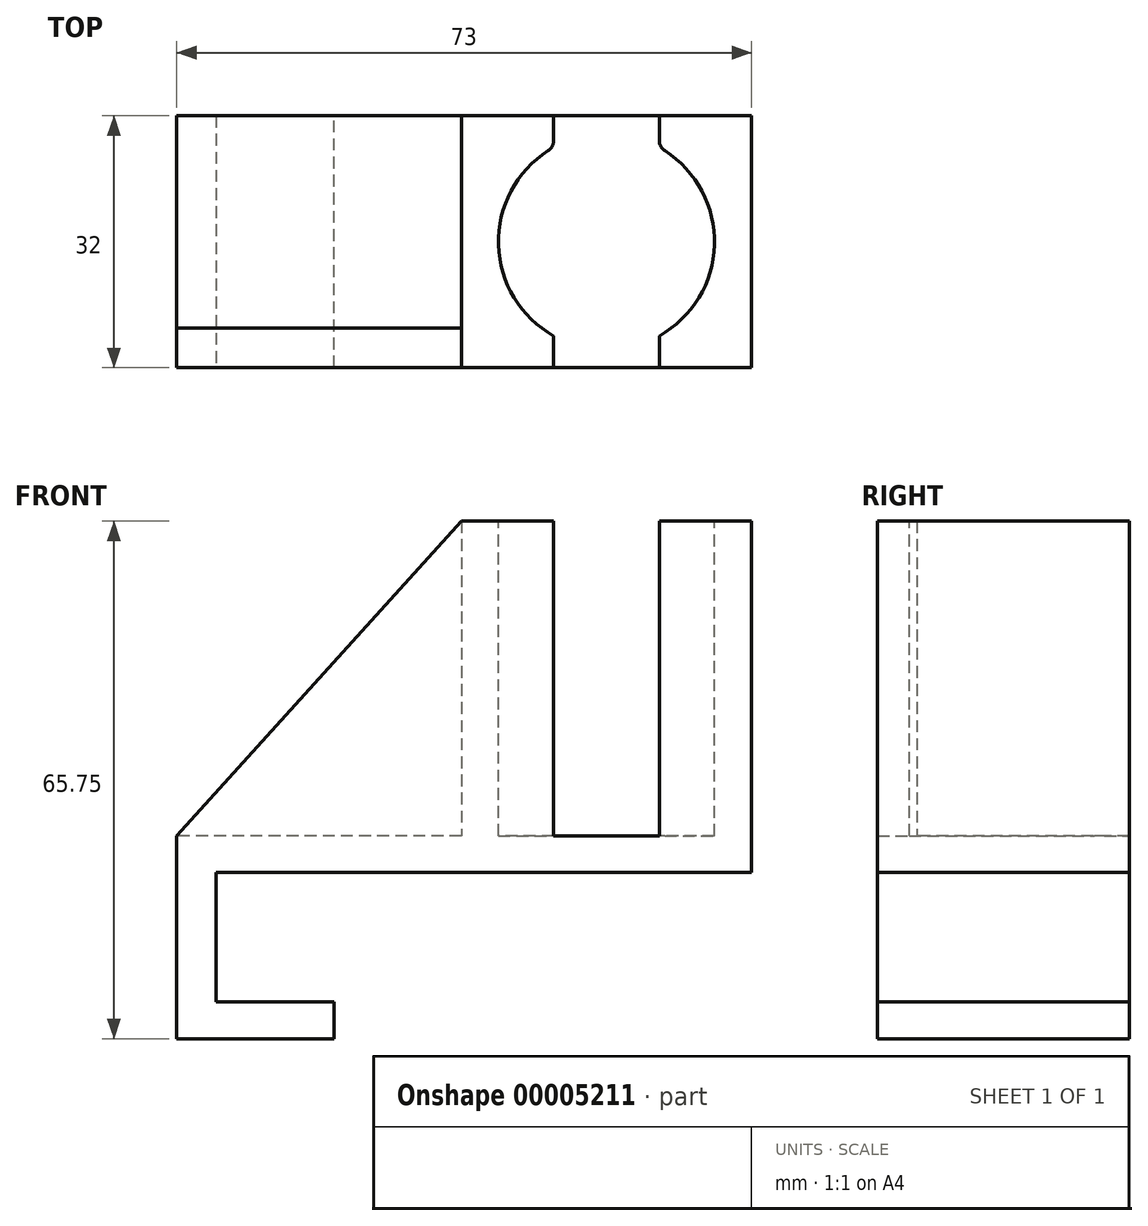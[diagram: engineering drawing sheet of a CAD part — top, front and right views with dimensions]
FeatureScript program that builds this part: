
annotation { "Feature Type Name" : "Feature", "Feature Type Description" : "" }
export const myFeature = defineFeature(function(context is Context, id is Id, definition is map)
    precondition{}
    {
        {
            var Q0;
            Q0=qCreatedBy(makeId("Front.planeOp"),FACE);
            var sketch = newSketch(context, id + "F0", { "sketchPlane" : qUnion([Q0])});
            skLineSegment(sketch, "E0.bottom", {"start": v(0, 0) * mm, "end": v(84, 0) * mm});
            skLineSegment(sketch, "E0.top", {"start": v(0, 15.75) * mm, "end": v(84, 15.75) * mm});
            skLineSegment(sketch, "E0.left", {"start": v(0, 0) * mm, "end": v(0, 15.75) * mm});
            skLineSegment(sketch, "E0.right", {"start": v(84, 0) * mm, "end": v(84, 15.75) * mm, "construction": true});
            skLineSegment(sketch, "E1", {"start": v(84, 15.75) * mm, "end": v(84, 20.75) * mm});
            skLineSegment(sketch, "E2", {"start": v(84, 20.75) * mm, "end": v(-5, 20.75) * mm});
            skLineSegment(sketch, "E3", {"start": v(-5, 20.75) * mm, "end": v(-5, -5) * mm});
            skLineSegment(sketch, "E4", {"start": v(-5, -5) * mm, "end": v(84, -5) * mm});
            skLineSegment(sketch, "E5", {"start": v(84, -5) * mm, "end": v(84, 0) * mm});
            skLineSegment(sketch, "E6", {"start": v(0, 15.75) * mm, "end": v(-5, 15.75) * mm, "construction": true});
            skSolve(sketch);
        }
        {
            var Q0;
            Q0 = qSketchRegion(id + "F0", true);
            extrude(context, id + "F1", {"entities" : qUnion([Q0]), "depth" : 32 * mm, "offsetDistance" : 25 * mm});
        }
        {
            var Q0;
            Q0=makeQuery(id+"F1.opExtrude","CAP_FACE",FACE,{"disambiguationData":[OSD([sQuery(id+"F0.wireOp",EDGE,"E0.bottom"),sQuery(id+"F0.wireOp",EDGE,"E0.top"),sQuery(id+"F0.wireOp",EDGE,"E0.left"),sQuery(id+"F0.wireOp",EDGE,"E1"),sQuery(id+"F0.wireOp",EDGE,"E2"),sQuery(id+"F0.wireOp",EDGE,"E3"),sQuery(id+"F0.wireOp",EDGE,"E4"),sQuery(id+"F0.wireOp",EDGE,"E5")])],"isStart":false});
            var sketch = newSketch(context, id + "F2", { "sketchPlane" : qUnion([Q0])});
            skLineSegment(sketch, "E7.bottom", {"start": v(84, 0) * mm, "end": v(15, 0) * mm});
            skLineSegment(sketch, "E7.top", {"start": v(84, -5) * mm, "end": v(15, -5) * mm});
            skLineSegment(sketch, "E7.left", {"start": v(84, 0) * mm, "end": v(84, -5) * mm});
            skLineSegment(sketch, "E7.right", {"start": v(15, 0) * mm, "end": v(15, -5) * mm});
            skSolve(sketch);
        }
        {
            var Q0;
            Q0 = qSketchRegion(id + "F2", true);
            extrude(context, id + "F3", {"entities" : qUnion([Q0]), "operationType" : NewBodyOperationType.REMOVE, "endBound" : BoundingType.THROUGH_ALL, "oppositeDirection" : true, "depth" : 25 * mm, "offsetDistance" : 25 * mm});
        }
        {
            var Q0;
            Q0=makeQuery(id+"F1.opExtrude","SWEPT_FACE",FACE,{"disambiguationData":[OSD([sQuery(id+"F0.wireOp",EDGE,"E2")])]});
            var sketch = newSketch(context, id + "F4", { "sketchPlane" : qUnion([Q0])});
            skCircle(sketch, "E8", {"center": v(49.58, -16) * mm, "radius": 13.43 * mm, "construction": true});
            skCircle(sketch, "E9", {"center": v(49.58, -16) * mm, "radius": 34.42 * mm, "construction": true});
            skLineSegment(sketch, "E10", {"start": v(49.58, -16) * mm, "end": v(15.15, -16) * mm, "construction": true});
            skLineSegment(sketch, "E11", {"start": v(15.15, -16) * mm, "end": v(-5, -16) * mm, "construction": true});
            skLineSegment(sketch, "E12", {"start": v(49.58, -16) * mm, "end": v(49.58, 0) * mm, "construction": true});
            skArc(sketch, "E13", {"start": v(42.86, -27.63) * mm, "mid": v(36.15, -16) * mm, "end": v(42.86, -4.37) * mm});
            skLineSegment(sketch, "E14", {"start": v(42.86, -4.37) * mm, "end": v(42.86, 0) * mm});
            skLineSegment(sketch, "E15", {"start": v(42.86, 0) * mm, "end": v(31.15, 0) * mm});
            skLineSegment(sketch, "E16", {"start": v(31.15, 0) * mm, "end": v(31.15, -32) * mm});
            skLineSegment(sketch, "E17", {"start": v(31.15, -32) * mm, "end": v(42.86, -32) * mm});
            skLineSegment(sketch, "E18", {"start": v(42.86, -32) * mm, "end": v(42.86, -27.63) * mm});
            skLineSegment(sketch, "E19", {"start": v(42.86, -4.37) * mm, "end": v(49.58, -16) * mm, "construction": true});
            skArc(sketch, "E20.MirrorCS", {"start": v(56.29, -27.63) * mm, "mid": v(63, -16) * mm, "end": v(56.29, -4.37) * mm});
            skLineSegment(sketch, "E21.MirrorCS", {"start": v(56.29, -32) * mm, "end": v(56.29, -27.63) * mm});
            skLineSegment(sketch, "E22.MirrorCS", {"start": v(68, -32) * mm, "end": v(56.29, -32) * mm});
            skLineSegment(sketch, "E23.MirrorCS", {"start": v(68, 0) * mm, "end": v(68, -32) * mm});
            skLineSegment(sketch, "E24.MirrorCS", {"start": v(56.29, 0) * mm, "end": v(68, 0) * mm});
            skLineSegment(sketch, "E25.MirrorCS", {"start": v(56.29, -4.37) * mm, "end": v(56.29, 0) * mm});
            skSolve(sketch);
        }
        {
            var Q0;
            Q0 = qSketchRegion(id + "F4", true);
            extrude(context, id + "F5", {"entities" : qUnion([Q0]), "operationType" : NewBodyOperationType.ADD, "depth" : 40 * mm, "offsetDistance" : 25 * mm});
        }
        {
            var Q0;
            Q0=makeQuery(id+"F5.boolean.opBoolean","MERGE",FACE,{"derivedFrom":[makeQuery(id+"F1.opExtrude","CAP_FACE",FACE,{"disambiguationData":[OSD([sQuery(id+"F0.wireOp",EDGE,"E0.bottom"),sQuery(id+"F0.wireOp",EDGE,"E0.top"),sQuery(id+"F0.wireOp",EDGE,"E0.left"),sQuery(id+"F0.wireOp",EDGE,"E1"),sQuery(id+"F0.wireOp",EDGE,"E2"),sQuery(id+"F0.wireOp",EDGE,"E3"),sQuery(id+"F0.wireOp",EDGE,"E4"),sQuery(id+"F0.wireOp",EDGE,"E5")])],"isStart":false}),makeQuery(id+"F5.opExtrude","SWEPT_FACE",FACE,{"disambiguationData":[OSD([sQuery(id+"F4.wireOp",EDGE,"E17")])]}),makeQuery(id+"F5.opExtrude","SWEPT_FACE",FACE,{"disambiguationData":[OSD([sQuery(id+"F4.wireOp",EDGE,"E22.MirrorCS")])]})]});
            var sketch = newSketch(context, id + "F6", { "sketchPlane" : qUnion([Q0])});
            skLineSegment(sketch, "E26.0", {"start": v(31.15, 60.75) * mm, "end": v(31.15, 20.75) * mm});
            skLineSegment(sketch, "E26.1", {"start": v(31.15, 20.75) * mm, "end": v(-5, 20.75) * mm});
            skLineSegment(sketch, "E27", {"start": v(31.15, 60.75) * mm, "end": v(-5, 20.75) * mm});
            skSolve(sketch);
        }
        {
            var Q0;
            Q0 = qSketchRegion(id + "F6", true);
            extrude(context, id + "F7", {"entities" : qUnion([Q0]), "operationType" : NewBodyOperationType.ADD, "oppositeDirection" : true, "depth" : 5 * mm, "offsetDistance" : 25 * mm});
        }
        {
            var Q0;
            Q0=makeQuery(id+"F1.opExtrude","SWEPT_FACE",FACE,{"disambiguationData":[OSD([sQuery(id+"F0.wireOp",EDGE,"E1")])]});
            var Q1;
            Q1=makeQuery(id+"F5.opExtrude","SWEPT_FACE",FACE,{"disambiguationData":[OSD([sQuery(id+"F4.wireOp",EDGE,"E23.MirrorCS")])]});
            extrude(context, id + "F8", {"entities" : qUnion([Q0]), "operationType" : NewBodyOperationType.REMOVE, "endBound" : BoundingType.UP_TO_SURFACE, "oppositeDirection" : true, "depth" : 25 * mm, "endBoundEntityFace" : qUnion([Q1]), "offsetDistance" : 25 * mm});
        }
        {
            var Q0;
            Q0=makeQuery(id+"F7.boolean.opBoolean","MERGE",FACE,{"derivedFrom":[makeQuery(id+"F5.boolean.opBoolean","MERGE",FACE,{"derivedFrom":[makeQuery(id+"F1.opExtrude","CAP_FACE",FACE,{"disambiguationData":[OSD([sQuery(id+"F0.wireOp",EDGE,"E0.bottom"),sQuery(id+"F0.wireOp",EDGE,"E0.top"),sQuery(id+"F0.wireOp",EDGE,"E0.left"),sQuery(id+"F0.wireOp",EDGE,"E1"),sQuery(id+"F0.wireOp",EDGE,"E2"),sQuery(id+"F0.wireOp",EDGE,"E3"),sQuery(id+"F0.wireOp",EDGE,"E4"),sQuery(id+"F0.wireOp",EDGE,"E5")])],"isStart":false}),makeQuery(id+"F5.opExtrude","SWEPT_FACE",FACE,{"disambiguationData":[OSD([sQuery(id+"F4.wireOp",EDGE,"E17")])]}),makeQuery(id+"F5.opExtrude","SWEPT_FACE",FACE,{"disambiguationData":[OSD([sQuery(id+"F4.wireOp",EDGE,"E22.MirrorCS")])]})]}),makeQuery(id+"F7.opExtrude","CAP_FACE",FACE,{"disambiguationData":[OSD([sQuery(id+"F6.wireOp",EDGE,"E26.0"),sQuery(id+"F6.wireOp",EDGE,"E26.1"),sQuery(id+"F6.wireOp",EDGE,"E27")])],"isStart":true})]});
            var sketch = newSketch(context, id + "F9", { "sketchPlane" : qUnion([Q0])});
            skLineSegment(sketch, "E28", {"start": v(7.5, 0) * mm, "end": v(7.5, 15.75) * mm, "construction": true});
            skLineSegment(sketch, "E29.bottom", {"start": v(15, 16.1) * mm, "end": v(0, 16.1) * mm});
            skLineSegment(sketch, "E29.top", {"start": v(15, -0.35) * mm, "end": v(0, -0.35) * mm});
            skLineSegment(sketch, "E29.left", {"start": v(15, 16.1) * mm, "end": v(15, -0.35) * mm, "construction": true});
            skLineSegment(sketch, "E29.right", {"start": v(0, 16.1) * mm, "end": v(0, -0.35) * mm});
            skPoint(sketch, "E29.middle", {"position": v(7.5, 7.87) * mm});
            skLineSegment(sketch, "E30", {"start": v(15, 16.1) * mm, "end": v(68, 16.1) * mm});
            skLineSegment(sketch, "E31", {"start": v(68, 16.1) * mm, "end": v(68, -0.35) * mm});
            skLineSegment(sketch, "E32", {"start": v(68, -0.35) * mm, "end": v(15, -0.35) * mm});
            skSolve(sketch);
        }
        {
            var Q0;
            Q0 = qSketchRegion(id + "F9", true);
            extrude(context, id + "F10", {"entities" : qUnion([Q0]), "operationType" : NewBodyOperationType.REMOVE, "endBound" : BoundingType.THROUGH_ALL, "oppositeDirection" : true, "depth" : 25 * mm, "offsetDistance" : 25 * mm});
        }
        {
            var Q0;
            Q0=makeQuery(id+"F5.opExtrude","CAP_FACE",FACE,{"disambiguationData":[OSD([sQuery(id+"F4.wireOp",EDGE,"E20.MirrorCS"),sQuery(id+"F4.wireOp",EDGE,"E21.MirrorCS"),sQuery(id+"F4.wireOp",EDGE,"E22.MirrorCS"),sQuery(id+"F4.wireOp",EDGE,"E23.MirrorCS"),sQuery(id+"F4.wireOp",EDGE,"E24.MirrorCS"),sQuery(id+"F4.wireOp",EDGE,"E25.MirrorCS")])],"isStart":false});
            var sketch = newSketch(context, id + "F11", { "sketchPlane" : qUnion([Q0])});
            skCircle(sketch, "E33", {"center": v(49.58, -16) * mm, "radius": 13.73 * mm});
            skSolve(sketch);
        }
        {
            var Q0;
            Q0 = qSketchRegion(id + "F11", true);
            var Q1;
            {var subQ3=sQuery(id+"F0.wireOp",EDGE,"E2");Q1=makeQuery(id+"F5.boolean.opBoolean","SPLIT",FACE,{"disambiguationData":[TD([makeQuery(id+"F5.opExtrude","SWEPT_FACE",FACE,{"disambiguationData":[OSD([sQuery(id+"F4.wireOp",EDGE,"E13")])]})])],"derivedFrom":makeQuery(id+"F1.opExtrude","SWEPT_FACE",FACE,{"disambiguationData":[OSD([subQ3])]})});}
            extrude(context, id + "F12", {"entities" : qUnion([Q0]), "operationType" : NewBodyOperationType.REMOVE, "endBound" : BoundingType.UP_TO_SURFACE, "oppositeDirection" : true, "depth" : 25 * mm, "endBoundEntityFace" : qUnion([Q1]), "offsetDistance" : 25 * mm});
        }
        {
            var Q0;
            Q0=makeQuery(id+"F12.boolean.opBoolean","INTERSECT",EDGE,{"derivedFrom":[makeQuery(id+"F5.opExtrude","SWEPT_FACE",FACE,{"disambiguationData":[OSD([sQuery(id+"F4.wireOp",EDGE,"E14")])]}),makeQuery(id+"F12.opExtrude","SWEPT_FACE",FACE,{"disambiguationData":[OSD([sQuery(id+"F11.wireOp",EDGE,"E33")])]})]});
            var Q1;
            Q1=makeQuery(id+"F12.boolean.opBoolean","INTERSECT",EDGE,{"derivedFrom":[makeQuery(id+"F5.opExtrude","SWEPT_FACE",FACE,{"disambiguationData":[OSD([sQuery(id+"F4.wireOp",EDGE,"E25.MirrorCS")])]}),makeQuery(id+"F12.opExtrude","SWEPT_FACE",FACE,{"disambiguationData":[OSD([sQuery(id+"F11.wireOp",EDGE,"E33")])]})]});
            fillet(context, id + "F13", {"entities" : qUnion([Q0, Q1]), "radius" : 1.5 * mm, "tangentPropagation" : true, "allowEdgeOverflow" : false});
        }
    });
